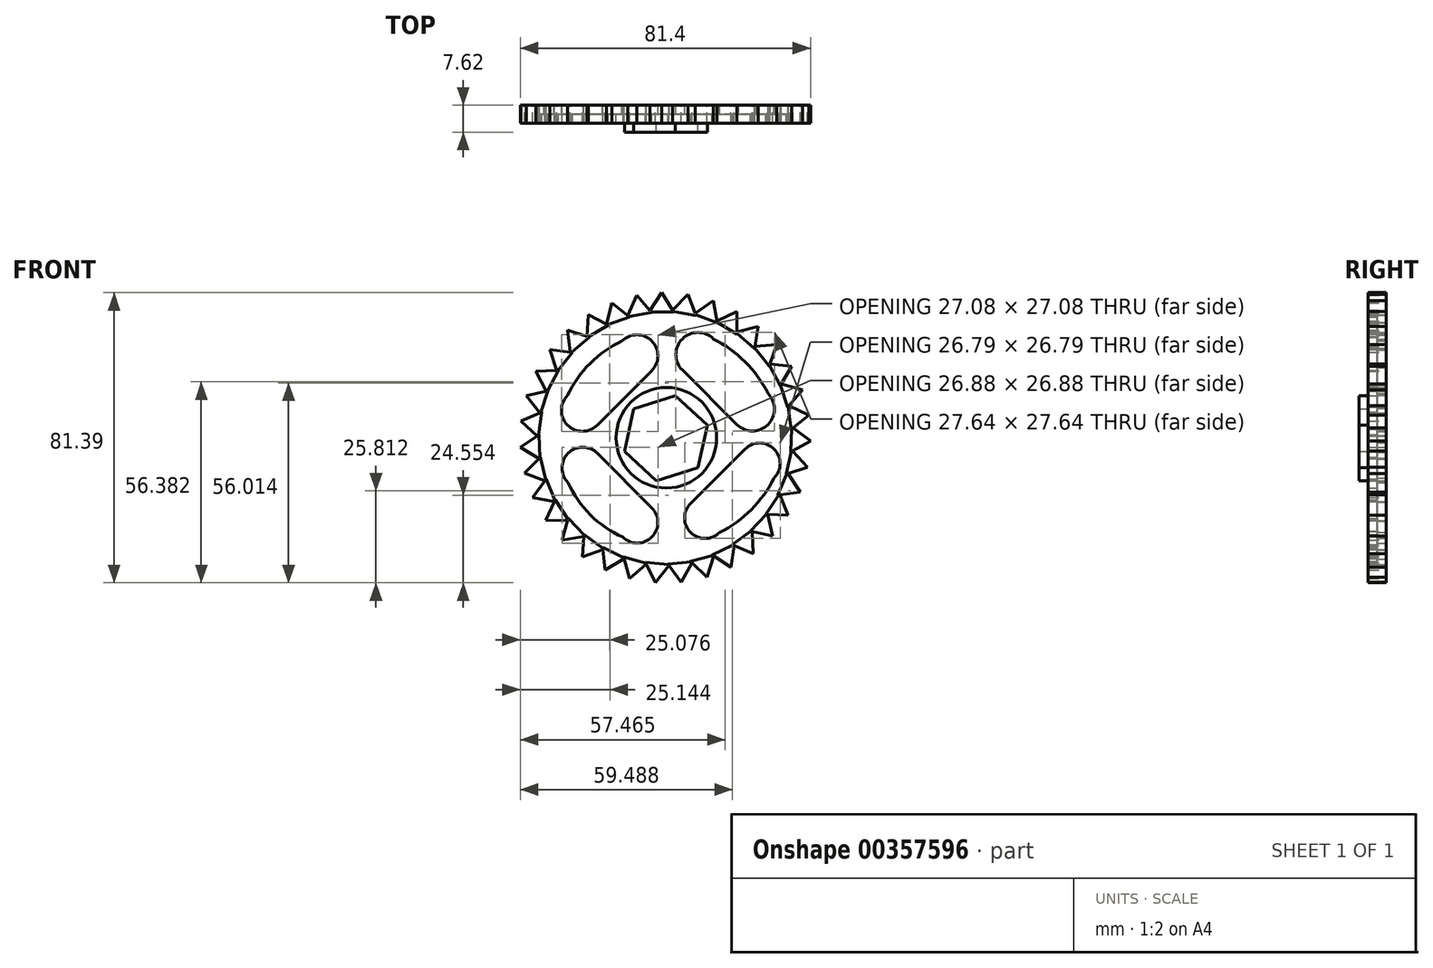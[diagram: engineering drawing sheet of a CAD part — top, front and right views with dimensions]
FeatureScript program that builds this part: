
annotation { "Feature Type Name" : "Feature", "Feature Type Description" : "" }
export const myFeature = defineFeature(function(context is Context, id is Id, definition is map)
    precondition{}
    {
        {
            var Q0;
            Q0=qCreatedBy(makeId("Front.planeOp"),FACE);
            var sketch = newSketch(context, id + "F0", { "sketchPlane" : qUnion([Q0])});
            skCircle(sketch, "E0.cCircle", {"center": v(-28.52, 27.1) * mm, "radius": 12.18 * mm, "construction": true});
            skLineSegment(sketch, "E0.0", {"start": v(-19.53, 18.88) * mm, "end": v(-31.15, 15.2) * mm});
            skLineSegment(sketch, "E0.1", {"start": v(-31.15, 15.2) * mm, "end": v(-40.14, 23.43) * mm});
            skLineSegment(sketch, "E0.2", {"start": v(-40.14, 23.43) * mm, "end": v(-37.51, 35.33) * mm});
            skLineSegment(sketch, "E0.3", {"start": v(-37.51, 35.33) * mm, "end": v(-25.9, 39) * mm});
            skLineSegment(sketch, "E0.4", {"start": v(-25.9, 39) * mm, "end": v(-16.9, 30.78) * mm});
            skLineSegment(sketch, "E0.5", {"start": v(-16.9, 30.78) * mm, "end": v(-19.53, 18.88) * mm});
            skSolve(sketch);
        }
        {
            var Q0;
            Q0=makeQuery(id+"F0.imprint","IMPRINT",FACE,{"disambiguationData":[TD([[makeQuery(id+"F0.imprint","IMPRINT",EDGE,{"derivedFrom":sQuery(id+"F0.wireOp",EDGE,"E0.0")}),-1.0]])]});
            extrude(context, id + "F1", {"entities" : qUnion([Q0]), "depth" : 7.62 * mm});
        }
        {
            var Q0;
            Q0=qCreatedBy(makeId("Front.planeOp"),FACE);
            var sketch = newSketch(context, id + "F2", { "sketchPlane" : qUnion([Q0])});
            skCircle(sketch, "E1", {"center": v(-28.9, 27.07) * mm, "radius": 35.75 * mm});
            skSolve(sketch);
        }
        {
            var Q0;
            Q0 = qSketchRegion(id + "F2", true);
            extrude(context, id + "F3", {"entities" : qUnion([Q0]), "operationType" : NewBodyOperationType.ADD, "depth" : 2.54 * mm});
        }
        {
            var Q0;
            Q0=qCreatedBy(makeId("Front.planeOp"),FACE);
            var sketch = newSketch(context, id + "F4", { "sketchPlane" : qUnion([Q0])});
            skLineSegment(sketch, "E2.bottom", {"start": v(-15.15, 54.96) * mm, "end": v(0.14, 39.68) * mm});
            skLineSegment(sketch, "E2.top", {"start": v(-23.89, 46.23) * mm, "end": v(-8.6, 30.94) * mm});
            skLineSegment(sketch, "E2.left", {"start": v(-15.15, 54.96) * mm, "end": v(-23.89, 46.23) * mm});
            skLineSegment(sketch, "E2.right", {"start": v(0.14, 39.68) * mm, "end": v(-8.6, 30.94) * mm});
            skArc(sketch, "E3", {"start": v(-8.6, 30.94) * mm, "mid": v(0.14, 30.94) * mm, "end": v(0.14, 39.68) * mm});
            skArc(sketch, "E4", {"start": v(-15.15, 54.96) * mm, "mid": v(-23.89, 54.96) * mm, "end": v(-23.89, 46.23) * mm});
            skLineSegment(sketch, "E5.bottom", {"start": v(-47.74, 22.87) * mm, "end": v(-32.45, 7.58) * mm});
            skLineSegment(sketch, "E5.top", {"start": v(-55.94, 14.67) * mm, "end": v(-40.65, -0.62) * mm});
            skLineSegment(sketch, "E5.left", {"start": v(-47.74, 22.87) * mm, "end": v(-55.94, 14.67) * mm});
            skLineSegment(sketch, "E5.right", {"start": v(-32.45, 7.58) * mm, "end": v(-40.65, -0.62) * mm});
            skArc(sketch, "E6", {"start": v(-40.65, -0.62) * mm, "mid": v(-32.45, -0.62) * mm, "end": v(-32.45, 7.58) * mm});
            skArc(sketch, "E7", {"start": v(-47.74, 22.87) * mm, "mid": v(-55.94, 22.87) * mm, "end": v(-55.94, 14.67) * mm});
            skLineSegment(sketch, "E8.bottom", {"start": v(-21.56, 8.8) * mm, "end": v(-6.28, 24.1) * mm});
            skLineSegment(sketch, "E8.top", {"start": v(-13.43, 0.67) * mm, "end": v(1.86, 15.96) * mm});
            skLineSegment(sketch, "E8.left", {"start": v(-21.56, 8.8) * mm, "end": v(-13.43, 0.67) * mm});
            skLineSegment(sketch, "E8.right", {"start": v(-6.28, 24.1) * mm, "end": v(1.86, 15.96) * mm});
            skArc(sketch, "E9", {"start": v(1.86, 15.96) * mm, "mid": v(1.86, 24.1) * mm, "end": v(-6.28, 24.1) * mm});
            skArc(sketch, "E10", {"start": v(-21.56, 8.8) * mm, "mid": v(-21.56, 0.67) * mm, "end": v(-13.43, 0.67) * mm});
            skLineSegment(sketch, "E11.bottom", {"start": v(-56.08, 39.11) * mm, "end": v(-40.8, 54.4) * mm});
            skLineSegment(sketch, "E11.top", {"start": v(-47.74, 30.77) * mm, "end": v(-32.45, 46.06) * mm});
            skLineSegment(sketch, "E11.left", {"start": v(-56.08, 39.11) * mm, "end": v(-47.74, 30.77) * mm});
            skLineSegment(sketch, "E11.right", {"start": v(-40.8, 54.4) * mm, "end": v(-32.45, 46.06) * mm});
            skArc(sketch, "E12", {"start": v(-32.45, 46.06) * mm, "mid": v(-32.45, 54.4) * mm, "end": v(-40.8, 54.4) * mm});
            skArc(sketch, "E13", {"start": v(-56.08, 39.11) * mm, "mid": v(-56.08, 30.77) * mm, "end": v(-47.74, 30.77) * mm});
            skArc(sketch, "E14", {"start": v(-40.8, 54.4) * mm, "mid": v(-49.77, 48.1) * mm, "end": v(-56.08, 39.11) * mm});
            skArc(sketch, "E15", {"start": v(0.14, 39.68) * mm, "mid": v(-6.27, 48.55) * mm, "end": v(-15.15, 54.96) * mm});
            skArc(sketch, "E16", {"start": v(-13.43, 0.67) * mm, "mid": v(-4.56, 7.1) * mm, "end": v(1.86, 15.96) * mm});
            skArc(sketch, "E17", {"start": v(-55.94, 14.67) * mm, "mid": v(-49.7, 5.62) * mm, "end": v(-40.65, -0.62) * mm});
            skSolve(sketch);
        }
        {
            var Q0;
            Q0 = qSketchRegion(id + "F4", true);
            extrude(context, id + "F5", {"entities" : qUnion([Q0]), "operationType" : NewBodyOperationType.REMOVE, "oppositeDirection" : true, "depth" : -2.54 * mm});
        }
        {
            var Q0;
            Q0=qCreatedBy(makeId("Front.planeOp"),FACE);
            var sketch = newSketch(context, id + "F6", { "sketchPlane" : qUnion([Q0])});
            skCircle(sketch, "E18", {"center": v(-28.68, 27.22) * mm, "radius": 16.64 * mm});
            skLineSegment(sketch, "E19", {"start": v(-29.63, 67.96) * mm, "end": v(-33.25, 62.54) * mm});
            skLineSegment(sketch, "E20", {"start": v(-33.25, 62.54) * mm, "end": v(-26.33, 62.54) * mm});
            skLineSegment(sketch, "E21", {"start": v(-26.33, 62.54) * mm, "end": v(-29.63, 67.96) * mm});
            skLineSegment(sketch, "E22.1.0", {"start": v(-20.06, 61.56) * mm, "end": v(-22.33, 67.48) * mm});
            skLineSegment(sketch, "E22.1.1", {"start": v(-22.33, 67.48) * mm, "end": v(-26.87, 62.8) * mm});
            skLineSegment(sketch, "E22.1.2", {"start": v(-26.87, 62.8) * mm, "end": v(-20.06, 61.56) * mm});
            skLineSegment(sketch, "E22.2.0", {"start": v(-14.06, 59.46) * mm, "end": v(-15.24, 65.7) * mm});
            skLineSegment(sketch, "E22.2.1", {"start": v(-15.24, 65.7) * mm, "end": v(-20.54, 61.9) * mm});
            skLineSegment(sketch, "E22.2.2", {"start": v(-20.54, 61.9) * mm, "end": v(-14.06, 59.46) * mm});
            skLineSegment(sketch, "E22.3.0", {"start": v(-8.53, 56.33) * mm, "end": v(-8.58, 62.67) * mm});
            skLineSegment(sketch, "E22.3.1", {"start": v(-8.58, 62.67) * mm, "end": v(-14.47, 59.89) * mm});
            skLineSegment(sketch, "E22.3.2", {"start": v(-14.47, 59.89) * mm, "end": v(-8.53, 56.33) * mm});
            skLineSegment(sketch, "E22.4.0", {"start": v(-3.65, 52.26) * mm, "end": v(-2.57, 58.51) * mm});
            skLineSegment(sketch, "E22.4.1", {"start": v(-2.57, 58.51) * mm, "end": v(-8.87, 56.82) * mm});
            skLineSegment(sketch, "E22.4.2", {"start": v(-8.87, 56.82) * mm, "end": v(-3.65, 52.26) * mm});
            skLineSegment(sketch, "E22.5.0", {"start": v(0.42, 47.39) * mm, "end": v(2.6, 53.34) * mm});
            skLineSegment(sketch, "E22.5.1", {"start": v(2.6, 53.34) * mm, "end": v(-3.9, 52.8) * mm});
            skLineSegment(sketch, "E22.5.2", {"start": v(-3.9, 52.8) * mm, "end": v(0.42, 47.39) * mm});
            skLineSegment(sketch, "E22.6.0", {"start": v(3.55, 41.87) * mm, "end": v(6.77, 47.33) * mm});
            skLineSegment(sketch, "E22.6.1", {"start": v(6.77, 47.33) * mm, "end": v(0.28, 47.97) * mm});
            skLineSegment(sketch, "E22.6.2", {"start": v(0.28, 47.97) * mm, "end": v(3.55, 41.87) * mm});
            skLineSegment(sketch, "E22.7.0", {"start": v(5.65, 35.87) * mm, "end": v(9.79, 40.68) * mm});
            skLineSegment(sketch, "E22.7.1", {"start": v(9.79, 40.68) * mm, "end": v(3.52, 42.46) * mm});
            skLineSegment(sketch, "E22.7.2", {"start": v(3.52, 42.46) * mm, "end": v(5.65, 35.87) * mm});
            skLineSegment(sketch, "E22.8.0", {"start": v(6.64, 29.6) * mm, "end": v(11.57, 33.59) * mm});
            skLineSegment(sketch, "E22.8.1", {"start": v(11.57, 33.59) * mm, "end": v(5.72, 36.46) * mm});
            skLineSegment(sketch, "E22.8.2", {"start": v(5.72, 36.46) * mm, "end": v(6.64, 29.6) * mm});
            skLineSegment(sketch, "E22.9.0", {"start": v(6.5, 23.25) * mm, "end": v(12.06, 26.3) * mm});
            skLineSegment(sketch, "E22.9.1", {"start": v(12.06, 26.3) * mm, "end": v(6.82, 30.16) * mm});
            skLineSegment(sketch, "E22.9.2", {"start": v(6.82, 30.16) * mm, "end": v(6.5, 23.25) * mm});
            skLineSegment(sketch, "E22.10.0", {"start": v(5.22, 17.03) * mm, "end": v(11.24, 19.03) * mm});
            skLineSegment(sketch, "E22.10.1", {"start": v(11.24, 19.03) * mm, "end": v(6.77, 23.77) * mm});
            skLineSegment(sketch, "E22.10.2", {"start": v(6.77, 23.77) * mm, "end": v(5.22, 17.03) * mm});
            skLineSegment(sketch, "E22.11.0", {"start": v(2.86, 11.13) * mm, "end": v(9.13, 12.02) * mm});
            skLineSegment(sketch, "E22.11.1", {"start": v(9.13, 12.02) * mm, "end": v(5.59, 17.5) * mm});
            skLineSegment(sketch, "E22.11.2", {"start": v(5.59, 17.5) * mm, "end": v(2.86, 11.13) * mm});
            skLineSegment(sketch, "E22.12.0", {"start": v(-0.53, 5.76) * mm, "end": v(5.8, 5.51) * mm});
            skLineSegment(sketch, "E22.12.1", {"start": v(5.8, 5.51) * mm, "end": v(3.3, 11.53) * mm});
            skLineSegment(sketch, "E22.12.2", {"start": v(3.3, 11.53) * mm, "end": v(-0.53, 5.76) * mm});
            skLineSegment(sketch, "E22.13.0", {"start": v(-4.82, 1.07) * mm, "end": v(1.37, -0.3) * mm});
            skLineSegment(sketch, "E22.13.1", {"start": v(1.37, -0.3) * mm, "end": v(-0.02, 6.07) * mm});
            skLineSegment(sketch, "E22.13.2", {"start": v(-0.02, 6.07) * mm, "end": v(-4.82, 1.07) * mm});
            skLineSegment(sketch, "E22.14.0", {"start": v(-9.87, -2.77) * mm, "end": v(-4.03, -5.23) * mm});
            skLineSegment(sketch, "E22.14.1", {"start": v(-4.03, -5.23) * mm, "end": v(-4.26, 1.29) * mm});
            skLineSegment(sketch, "E22.14.2", {"start": v(-4.26, 1.29) * mm, "end": v(-9.87, -2.77) * mm});
            skLineSegment(sketch, "E22.15.0", {"start": v(-15.54, -5.65) * mm, "end": v(-10.22, -9.11) * mm});
            skLineSegment(sketch, "E22.15.1", {"start": v(-10.22, -9.11) * mm, "end": v(-9.3, -2.66) * mm});
            skLineSegment(sketch, "E22.15.2", {"start": v(-9.3, -2.66) * mm, "end": v(-15.54, -5.65) * mm});
            skLineSegment(sketch, "E22.16.0", {"start": v(-21.62, -7.47) * mm, "end": v(-17.01, -11.82) * mm});
            skLineSegment(sketch, "E22.16.1", {"start": v(-17.01, -11.82) * mm, "end": v(-14.94, -5.64) * mm});
            skLineSegment(sketch, "E22.16.2", {"start": v(-14.94, -5.64) * mm, "end": v(-21.62, -7.47) * mm});
            skLineSegment(sketch, "E22.17.0", {"start": v(-27.93, -8.17) * mm, "end": v(-24.18, -13.28) * mm});
            skLineSegment(sketch, "E22.17.1", {"start": v(-24.18, -13.28) * mm, "end": v(-21.04, -7.57) * mm});
            skLineSegment(sketch, "E22.17.2", {"start": v(-21.04, -7.57) * mm, "end": v(-27.93, -8.17) * mm});
            skLineSegment(sketch, "E22.18.0", {"start": v(-34.27, -7.73) * mm, "end": v(-31.49, -13.43) * mm});
            skLineSegment(sketch, "E22.18.1", {"start": v(-31.49, -13.43) * mm, "end": v(-27.38, -8.37) * mm});
            skLineSegment(sketch, "E22.18.2", {"start": v(-27.38, -8.37) * mm, "end": v(-34.27, -7.73) * mm});
            skLineSegment(sketch, "E22.19.0", {"start": v(-40.43, -6.17) * mm, "end": v(-38.7, -12.27) * mm});
            skLineSegment(sketch, "E22.19.1", {"start": v(-38.7, -12.27) * mm, "end": v(-33.76, -8.03) * mm});
            skLineSegment(sketch, "E22.19.2", {"start": v(-33.76, -8.03) * mm, "end": v(-40.43, -6.17) * mm});
            skLineSegment(sketch, "E22.20.0", {"start": v(-46.2, -3.53) * mm, "end": v(-45.6, -9.85) * mm});
            skLineSegment(sketch, "E22.20.1", {"start": v(-45.6, -9.85) * mm, "end": v(-39.98, -6.55) * mm});
            skLineSegment(sketch, "E22.20.2", {"start": v(-39.98, -6.55) * mm, "end": v(-46.2, -3.53) * mm});
            skLineSegment(sketch, "E22.21.0", {"start": v(-51.42, 0.1) * mm, "end": v(-51.96, -6.22) * mm});
            skLineSegment(sketch, "E22.21.1", {"start": v(-51.96, -6.22) * mm, "end": v(-45.83, -4) * mm});
            skLineSegment(sketch, "E22.21.2", {"start": v(-45.83, -4) * mm, "end": v(-51.42, 0.1) * mm});
            skLineSegment(sketch, "E22.22.0", {"start": v(-55.9, 4.6) * mm, "end": v(-57.56, -1.53) * mm});
            skLineSegment(sketch, "E22.22.1", {"start": v(-57.56, -1.53) * mm, "end": v(-51.13, -0.42) * mm});
            skLineSegment(sketch, "E22.22.2", {"start": v(-51.13, -0.42) * mm, "end": v(-55.9, 4.6) * mm});
            skLineSegment(sketch, "E22.23.0", {"start": v(-59.5, 9.83) * mm, "end": v(-62.23, 4.1) * mm});
            skLineSegment(sketch, "E22.23.1", {"start": v(-62.23, 4.1) * mm, "end": v(-55.71, 4.03) * mm});
            skLineSegment(sketch, "E22.23.2", {"start": v(-55.71, 4.03) * mm, "end": v(-59.5, 9.83) * mm});
            skLineSegment(sketch, "E22.24.0", {"start": v(-62.12, 15.61) * mm, "end": v(-65.82, 10.47) * mm});
            skLineSegment(sketch, "E22.24.1", {"start": v(-65.82, 10.47) * mm, "end": v(-59.42, 9.24) * mm});
            skLineSegment(sketch, "E22.24.2", {"start": v(-59.42, 9.24) * mm, "end": v(-62.12, 15.61) * mm});
            skLineSegment(sketch, "E22.25.0", {"start": v(-63.65, 21.78) * mm, "end": v(-68.22, 17.37) * mm});
            skLineSegment(sketch, "E22.25.1", {"start": v(-68.22, 17.37) * mm, "end": v(-62.14, 15.02) * mm});
            skLineSegment(sketch, "E22.25.2", {"start": v(-62.14, 15.02) * mm, "end": v(-63.65, 21.78) * mm});
            skLineSegment(sketch, "E22.26.0", {"start": v(-64.06, 28.12) * mm, "end": v(-69.34, 24.6) * mm});
            skLineSegment(sketch, "E22.26.1", {"start": v(-69.34, 24.6) * mm, "end": v(-63.78, 21.2) * mm});
            skLineSegment(sketch, "E22.26.2", {"start": v(-63.78, 21.2) * mm, "end": v(-64.06, 28.12) * mm});
            skLineSegment(sketch, "E22.27.0", {"start": v(-63.34, 34.43) * mm, "end": v(-69.16, 31.9) * mm});
            skLineSegment(sketch, "E22.27.1", {"start": v(-69.16, 31.9) * mm, "end": v(-64.3, 27.57) * mm});
            skLineSegment(sketch, "E22.27.2", {"start": v(-64.3, 27.57) * mm, "end": v(-63.34, 34.43) * mm});
            skLineSegment(sketch, "E22.28.0", {"start": v(-61.5, 40.5) * mm, "end": v(-67.67, 39.07) * mm});
            skLineSegment(sketch, "E22.28.1", {"start": v(-67.67, 39.07) * mm, "end": v(-63.66, 33.93) * mm});
            skLineSegment(sketch, "E22.28.2", {"start": v(-63.66, 33.93) * mm, "end": v(-61.5, 40.5) * mm});
            skLineSegment(sketch, "E22.29.0", {"start": v(-58.59, 46.15) * mm, "end": v(-64.92, 45.84) * mm});
            skLineSegment(sketch, "E22.29.1", {"start": v(-64.92, 45.84) * mm, "end": v(-61.9, 40.07) * mm});
            skLineSegment(sketch, "E22.29.2", {"start": v(-61.9, 40.07) * mm, "end": v(-58.59, 46.15) * mm});
            skLineSegment(sketch, "E22.anchor1", {"start": v(-28.68, 27.22) * mm, "end": v(-33.25, 62.54) * mm, "construction": true});
            skLineSegment(sketch, "E22.anchor2", {"start": v(-28.68, 27.22) * mm, "end": v(-39.32, 61.21) * mm, "construction": true});
            skLineSegment(sketch, "E23.3.30.0", {"start": v(-61.01, 52.02) * mm, "end": v(-59.06, 45.8) * mm});
            skLineSegment(sketch, "E23.5.30.0", {"start": v(-54.72, 51.2) * mm, "end": v(-61.01, 52.02) * mm});
            skLineSegment(sketch, "E23.6.30.0", {"start": v(-59.06, 45.8) * mm, "end": v(-54.72, 51.2) * mm});
            skLineSegment(sketch, "E23.3.31.0", {"start": v(-56.06, 57.4) * mm, "end": v(-55.26, 50.93) * mm});
            skLineSegment(sketch, "E23.5.31.0", {"start": v(-50.02, 55.46) * mm, "end": v(-56.06, 57.4) * mm});
            skLineSegment(sketch, "E23.6.31.0", {"start": v(-55.26, 50.93) * mm, "end": v(-50.02, 55.46) * mm});
            skLineSegment(sketch, "E23.3.32.0", {"start": v(-50.23, 61.8) * mm, "end": v(-50.6, 55.3) * mm});
            skLineSegment(sketch, "E23.5.32.0", {"start": v(-44.63, 58.82) * mm, "end": v(-50.23, 61.8) * mm});
            skLineSegment(sketch, "E23.6.32.0", {"start": v(-50.6, 55.3) * mm, "end": v(-44.63, 58.82) * mm});
            skLineSegment(sketch, "E23.3.33.0", {"start": v(-43.7, 65.1) * mm, "end": v(-45.22, 58.76) * mm});
            skLineSegment(sketch, "E23.5.33.0", {"start": v(-38.73, 61.17) * mm, "end": v(-43.7, 65.1) * mm});
            skLineSegment(sketch, "E23.6.33.0", {"start": v(-45.22, 58.76) * mm, "end": v(-38.73, 61.17) * mm});
            skLineSegment(sketch, "E23.3.34.0", {"start": v(-36.69, 67.18) * mm, "end": v(-39.32, 61.21) * mm});
            skLineSegment(sketch, "E23.5.34.0", {"start": v(-32.5, 62.42) * mm, "end": v(-36.69, 67.18) * mm});
            skLineSegment(sketch, "E23.6.34.0", {"start": v(-39.32, 61.21) * mm, "end": v(-32.5, 62.42) * mm});
            skCircle(sketch, "E24", {"center": v(-28.68, 27.22) * mm, "radius": 16.8 * mm});
            skSolve(sketch);
        }
        {
            var Q0;
            Q0 = qSketchRegion(id + "F6", true);
            extrude(context, id + "F7", {"entities" : qUnion([Q0]), "operationType" : NewBodyOperationType.ADD, "depth" : 5.08 * mm});
        }
        {
            var Q0;
            Q0=qCreatedBy(makeId("Front.planeOp"),FACE);
            var sketch = newSketch(context, id + "F8", { "sketchPlane" : qUnion([Q0])});
            skCircle(sketch, "E25", {"center": v(-28.35, 27.23) * mm, "radius": 14.1 * mm});
            skSolve(sketch);
        }
        {
            var Q0;
            Q0 = qSketchRegion(id + "F8", true);
            extrude(context, id + "F9", {"entities" : qUnion([Q0]), "operationType" : NewBodyOperationType.ADD, "depth" : 5.08 * mm});
        }
    });
